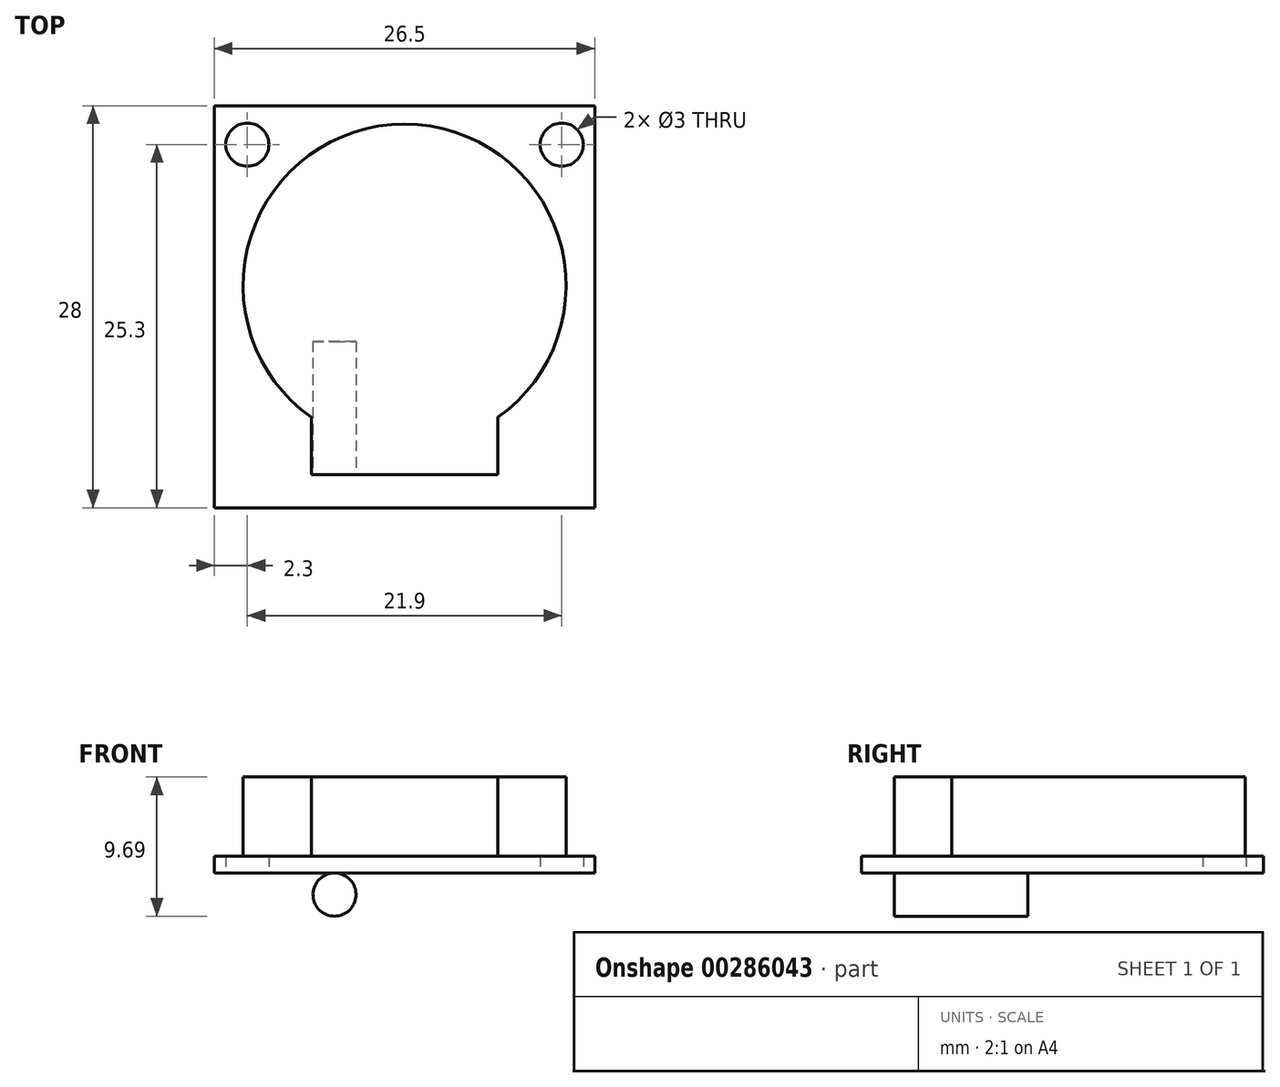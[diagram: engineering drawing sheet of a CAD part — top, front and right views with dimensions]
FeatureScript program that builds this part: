
annotation { "Feature Type Name" : "Feature", "Feature Type Description" : "" }
export const myFeature = defineFeature(function(context is Context, id is Id, definition is map)
    precondition{}
    {
        {
            var Q0;
            Q0=qCreatedBy(makeId("Top.planeOp"),FACE);
            var sketch = newSketch(context, id + "F0", { "sketchPlane" : qUnion([Q0])});
            skLineSegment(sketch, "E0.bottom", {"start": v(-13.25, 14) * mm, "end": v(13.25, 14) * mm});
            skLineSegment(sketch, "E0.top", {"start": v(-13.25, -14) * mm, "end": v(13.25, -14) * mm});
            skLineSegment(sketch, "E0.left", {"start": v(-13.25, 14) * mm, "end": v(-13.25, -14) * mm});
            skLineSegment(sketch, "E0.right", {"start": v(13.25, 14) * mm, "end": v(13.25, -14) * mm});
            skCircle(sketch, "E1", {"center": v(-10.95, 11.3) * mm, "radius": 1.5 * mm});
            skCircle(sketch, "E2", {"center": v(10.95, 11.3) * mm, "radius": 1.5 * mm});
            skSolve(sketch);
        }
        {
            var Q0;
            Q0=makeQuery(id+"F0.imprint","IMPRINT",FACE,{"disambiguationData":[TD([[makeQuery(id+"F0.imprint","IMPRINT",EDGE,{"derivedFrom":sQuery(id+"F0.wireOp",EDGE,"E0.bottom")}),-1.0]])]});
            extrude(context, id + "F1", {"entities" : qUnion([Q0]), "depth" : 1.2 * mm});
        }
        {
            var Q0;
            Q0=makeQuery(id+"F1.opExtrude","CAP_FACE",FACE,{"disambiguationData":[OSD([sQuery(id+"F0.wireOp",EDGE,"E0.bottom"),sQuery(id+"F0.wireOp",EDGE,"E0.top"),sQuery(id+"F0.wireOp",EDGE,"E0.left"),sQuery(id+"F0.wireOp",EDGE,"E0.right"),sQuery(id+"F0.wireOp",EDGE,"E1"),sQuery(id+"F0.wireOp",EDGE,"E2")])],"isStart":false});
            var sketch = newSketch(context, id + "F2", { "sketchPlane" : qUnion([Q0])});
            skArc(sketch, "E3", {"start": v(6.5, -7.7) * mm, "mid": v(0, 12.73) * mm, "end": v(-6.5, -7.7) * mm});
            skLineSegment(sketch, "E4.bottom", {"start": v(-6.5, -11.7) * mm, "end": v(6.5, -11.7) * mm});
            skLineSegment(sketch, "E4.left", {"start": v(-6.5, -11.7) * mm, "end": v(-6.5, -7.7) * mm});
            skLineSegment(sketch, "E4.right", {"start": v(6.5, -11.7) * mm, "end": v(6.5, -7.7) * mm});
            skSolve(sketch);
        }
        {
            var Q0;
            Q0 = qSketchRegion(id + "F2", true);
            extrude(context, id + "F3", {"entities" : qUnion([Q0]), "operationType" : NewBodyOperationType.ADD, "depth" : 5.5 * mm});
        }
        {
            var Q0;
            Q0=makeQuery(id+"F3.opExtrude","SWEPT_FACE",FACE,{"disambiguationData":[OSD([sQuery(id+"F2.wireOp",EDGE,"E4.bottom")])]});
            var sketch = newSketch(context, id + "F4", { "sketchPlane" : qUnion([Q0])});
            skCircle(sketch, "E5", {"center": v(-4.88, -1.49) * mm, "radius": 1.5 * mm});
            skSolve(sketch);
        }
        {
            var Q0;
            Q0 = qSketchRegion(id + "F4", true);
            extrude(context, id + "F5", {"entities" : qUnion([Q0]), "oppositeDirection" : true, "depth" : 9.3 * mm});
        }
    });
